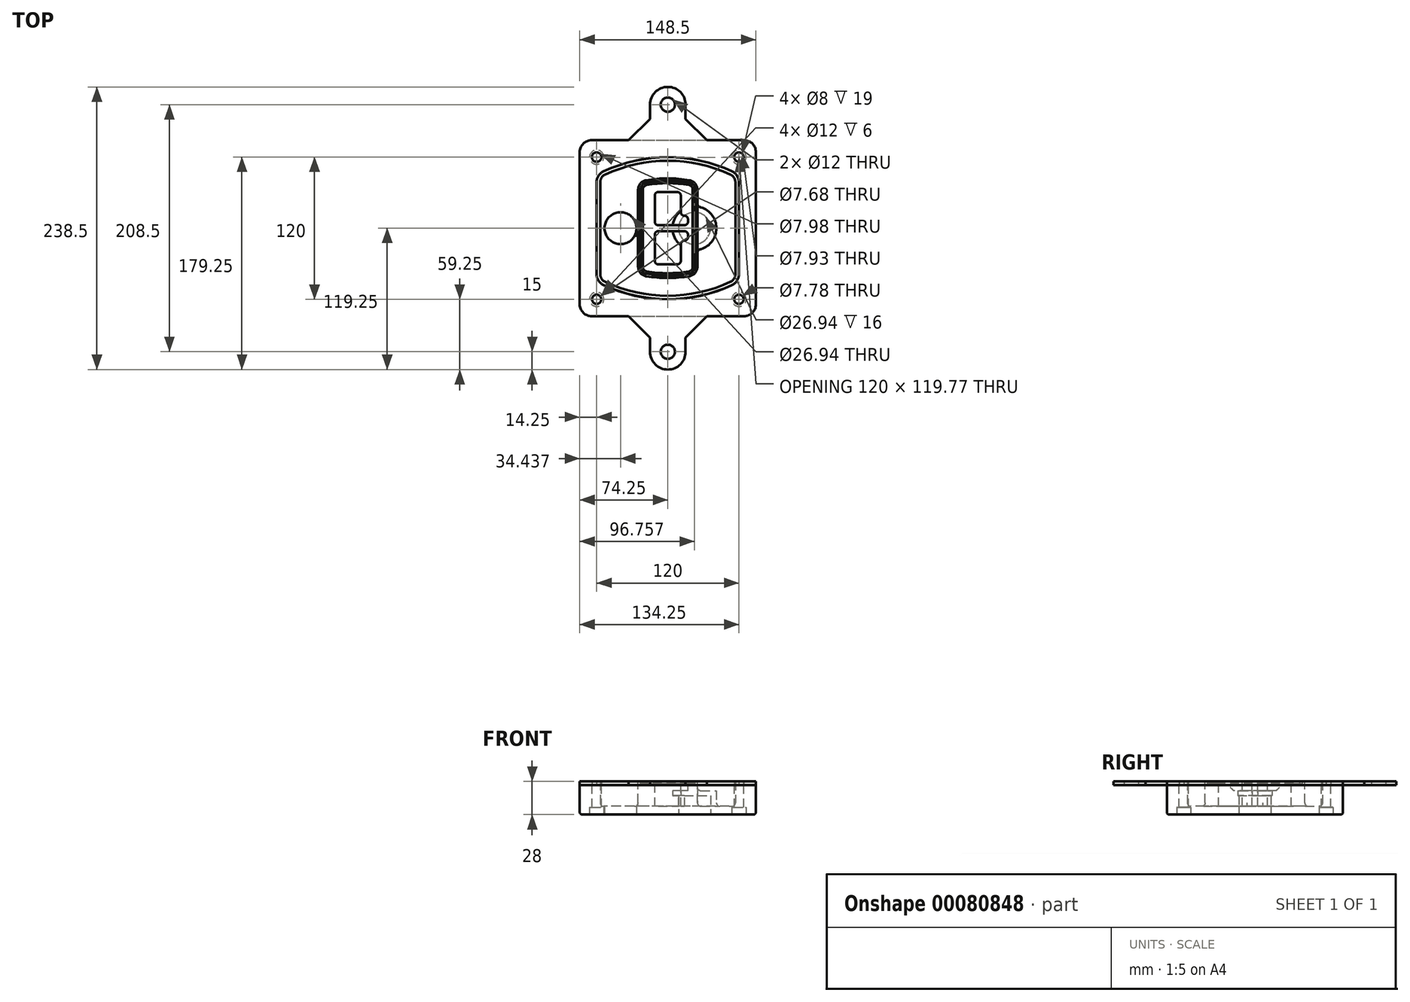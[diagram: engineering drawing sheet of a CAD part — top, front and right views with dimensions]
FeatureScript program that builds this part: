
annotation { "Feature Type Name" : "Feature", "Feature Type Description" : "" }
export const myFeature = defineFeature(function(context is Context, id is Id, definition is map)
    precondition{}
    {
        {
            var Q0;
            Q0=qCreatedBy(makeId("Top.planeOp"),FACE);
            var sketch = newSketch(context, id + "F0", { "sketchPlane" : qUnion([Q0])});
            skPoint(sketch, "E0.rect.middle", {"position": v(0, 0) * mm});
            skLineSegment(sketch, "E1.bottom", {"start": v(-64.25, -74.25) * mm, "end": v(64.25, -74.25) * mm});
            skLineSegment(sketch, "E1.top", {"start": v(-64.25, 74.25) * mm, "end": v(64.25, 74.25) * mm});
            skLineSegment(sketch, "E1.left", {"start": v(-74.25, -64.25) * mm, "end": v(-74.25, 64.25) * mm});
            skLineSegment(sketch, "E1.right", {"start": v(74.25, -64.25) * mm, "end": v(74.25, 64.25) * mm});
            skLineSegment(sketch, "E2", {"start": v(-74.25, 74.25) * mm, "end": v(74.25, -74.25) * mm, "construction": true});
            skLineSegment(sketch, "E3", {"start": v(74.25, 74.25) * mm, "end": v(-74.25, -74.25) * mm, "construction": true});
            skCircle(sketch, "E4", {"center": v(-60, 60) * mm, "radius": 4 * mm});
            skCircle(sketch, "E5", {"center": v(60, 60) * mm, "radius": 4 * mm});
            skCircle(sketch, "E6", {"center": v(60, -60) * mm, "radius": 4 * mm});
            skCircle(sketch, "E7", {"center": v(-60, -60) * mm, "radius": 4 * mm});
            skLineSegment(sketch, "E8", {"start": v(-60, 60) * mm, "end": v(60, 60) * mm, "construction": true});
            skLineSegment(sketch, "E9", {"start": v(60, 60) * mm, "end": v(60, -60) * mm, "construction": true});
            skLineSegment(sketch, "E10", {"start": v(60, -60) * mm, "end": v(-60, -60) * mm, "construction": true});
            skLineSegment(sketch, "E11", {"start": v(-60, -60) * mm, "end": v(-60, 60) * mm, "construction": true});
            skLineSegment(sketch, "E12", {"start": v(-60, 38.83) * mm, "end": v(-60, -38.83) * mm});
            skLineSegment(sketch, "E13", {"start": v(60, 38.83) * mm, "end": v(60, -38.83) * mm});
            skArc(sketch, "E14", {"start": v(54.26, 47.88) * mm, "mid": v(0, 60) * mm, "end": v(-54.26, 47.88) * mm});
            skArc(sketch, "E15", {"start": v(-54.26, -47.88) * mm, "mid": v(0, -60) * mm, "end": v(54.26, -47.88) * mm});
            skLineSegment(sketch, "E16", {"start": v(-60, 0) * mm, "end": v(60, 0) * mm, "construction": true});
            skPoint(sketch, "E17.visualSharp", {"position": v(-60, -45) * mm});
            skArc(sketch, "E17.filletArc", {"start": v(-60, -38.83) * mm, "mid": v(-58.44, -44.2) * mm, "end": v(-54.26, -47.88) * mm});
            skPoint(sketch, "E18.visualSharp", {"position": v(-60, 45) * mm});
            skArc(sketch, "E18.filletArc", {"start": v(-54.26, 47.88) * mm, "mid": v(-58.44, 44.2) * mm, "end": v(-60, 38.83) * mm});
            skPoint(sketch, "E19.visualSharp", {"position": v(60, 45) * mm});
            skArc(sketch, "E19.filletArc", {"start": v(60, 38.83) * mm, "mid": v(58.44, 44.2) * mm, "end": v(54.26, 47.88) * mm});
            skPoint(sketch, "E20.visualSharp", {"position": v(60, -45) * mm});
            skArc(sketch, "E20.filletArc", {"start": v(54.26, -47.88) * mm, "mid": v(58.44, -44.2) * mm, "end": v(60, -38.83) * mm});
            skPoint(sketch, "E21.visualSharp", {"position": v(-74.25, 74.25) * mm});
            skArc(sketch, "E21.filletArc", {"start": v(-64.25, 74.25) * mm, "mid": v(-71.32, 71.32) * mm, "end": v(-74.25, 64.25) * mm});
            skPoint(sketch, "E22.visualSharp", {"position": v(74.25, 74.25) * mm});
            skArc(sketch, "E22.filletArc", {"start": v(74.25, 64.25) * mm, "mid": v(71.32, 71.32) * mm, "end": v(64.25, 74.25) * mm});
            skPoint(sketch, "E23.visualSharp", {"position": v(74.25, -74.25) * mm});
            skArc(sketch, "E23.filletArc", {"start": v(64.25, -74.25) * mm, "mid": v(71.32, -71.32) * mm, "end": v(74.25, -64.25) * mm});
            skPoint(sketch, "E24.visualSharp", {"position": v(-74.25, -74.25) * mm});
            skArc(sketch, "E24.filletArc", {"start": v(-74.25, -64.25) * mm, "mid": v(-71.32, -71.32) * mm, "end": v(-64.25, -74.25) * mm});
            skArc(sketch, "E25.0", {"start": v(57, 38.83) * mm, "mid": v(55.9, 42.58) * mm, "end": v(52.98, 45.17) * mm});
            skLineSegment(sketch, "E25.1", {"start": v(57, 38.83) * mm, "end": v(57, -38.83) * mm});
            skArc(sketch, "E25.2", {"start": v(52.98, -45.17) * mm, "mid": v(55.9, -42.58) * mm, "end": v(57, -38.83) * mm});
            skArc(sketch, "E25.3", {"start": v(-52.98, -45.17) * mm, "mid": v(0, -57) * mm, "end": v(52.98, -45.17) * mm});
            skArc(sketch, "E25.4", {"start": v(-57, -38.83) * mm, "mid": v(-55.9, -42.58) * mm, "end": v(-52.98, -45.17) * mm});
            skArc(sketch, "E25.5", {"start": v(52.98, 45.17) * mm, "mid": v(0, 57) * mm, "end": v(-52.98, 45.17) * mm});
            skLineSegment(sketch, "E25.6", {"start": v(-57, 38.83) * mm, "end": v(-57, -38.83) * mm});
            skArc(sketch, "E25.7", {"start": v(-52.98, 45.17) * mm, "mid": v(-55.9, 42.58) * mm, "end": v(-57, 38.83) * mm});
            skArc(sketch, "E26.0", {"start": v(-55.96, 51.5) * mm, "mid": v(-61.82, 46.33) * mm, "end": v(-64, 38.83) * mm});
            skArc(sketch, "E26.1", {"start": v(55.96, 51.5) * mm, "mid": v(0, 64) * mm, "end": v(-55.96, 51.5) * mm});
            skArc(sketch, "E26.2", {"start": v(64, 38.83) * mm, "mid": v(61.82, 46.33) * mm, "end": v(55.96, 51.5) * mm});
            skLineSegment(sketch, "E26.3", {"start": v(64, 38.83) * mm, "end": v(64, -38.83) * mm});
            skArc(sketch, "E26.4", {"start": v(55.96, -51.5) * mm, "mid": v(61.82, -46.33) * mm, "end": v(64, -38.83) * mm});
            skLineSegment(sketch, "E26.5", {"start": v(-64, 38.83) * mm, "end": v(-64, -38.83) * mm});
            skArc(sketch, "E26.6", {"start": v(-55.96, -51.5) * mm, "mid": v(0, -64) * mm, "end": v(55.96, -51.5) * mm});
            skArc(sketch, "E26.7", {"start": v(-64, -38.83) * mm, "mid": v(-61.82, -46.33) * mm, "end": v(-55.96, -51.5) * mm});
            skSolve(sketch);
        }
        {
            var Q0;
            Q0=makeQuery(id+"F0.imprint","IMPRINT",FACE,{"disambiguationData":[TD([[makeQuery(id+"F0.imprint","IMPRINT",EDGE,{"derivedFrom":sQuery(id+"F0.wireOp",EDGE,"E1.bottom")}),1.0]])]});
            var Q1;
            Q1=makeQuery(id+"F0.imprint","IMPRINT",FACE,{"disambiguationData":[TD([[makeQuery(id+"F0.imprint","IMPRINT",EDGE,{"derivedFrom":sQuery(id+"F0.wireOp",EDGE,"E12")}),1.0]])]});
            var Q2;
            Q2=makeQuery(id+"F0.imprint","IMPRINT",FACE,{"disambiguationData":[TD([[makeQuery(id+"F0.imprint","IMPRINT",EDGE,{"derivedFrom":sQuery(id+"F0.wireOp",EDGE,"E25.0")}),1.0]])]});
            var Q3;
            Q3=makeQuery(id+"F0.imprint","IMPRINT",FACE,{"disambiguationData":[TD([[makeQuery(id+"F0.imprint","IMPRINT",EDGE,{"derivedFrom":sQuery(id+"F0.wireOp",EDGE,"E12")}),-1.0]])]});
            extrude(context, id + "F1", {"entities" : qUnion([Q0, Q1, Q2, Q3]), "oppositeDirection" : true, "depth" : 25 * mm});
        }
        {
            var Q0;
            Q0=makeQuery(id+"F0.imprint","IMPRINT",FACE,{"disambiguationData":[TD([[makeQuery(id+"F0.imprint","IMPRINT",EDGE,{"derivedFrom":sQuery(id+"F0.wireOp",EDGE,"E12")}),1.0]])]});
            extrude(context, id + "F2", {"entities" : qUnion([Q0]), "operationType" : NewBodyOperationType.ADD, "depth" : 3 * mm});
        }
        {
            var Q0;
            Q0=makeQuery(id+"F0.imprint","IMPRINT",FACE,{"disambiguationData":[TD([[makeQuery(id+"F0.imprint","IMPRINT",EDGE,{"derivedFrom":sQuery(id+"F0.wireOp",EDGE,"E25.0")}),1.0]])]});
            extrude(context, id + "F3", {"entities" : qUnion([Q0]), "operationType" : NewBodyOperationType.REMOVE, "oppositeDirection" : true, "depth" : 18 * mm});
        }
        {
            var Q0;
            Q0=makeQuery(id+"F2.opExtrude","CAP_FACE",FACE,{"disambiguationData":[OSD([sQuery(id+"F0.wireOp",EDGE,"E12"),sQuery(id+"F0.wireOp",EDGE,"E13"),sQuery(id+"F0.wireOp",EDGE,"E14"),sQuery(id+"F0.wireOp",EDGE,"E15"),sQuery(id+"F0.wireOp",EDGE,"E17.filletArc"),sQuery(id+"F0.wireOp",EDGE,"E18.filletArc"),sQuery(id+"F0.wireOp",EDGE,"E19.filletArc"),sQuery(id+"F0.wireOp",EDGE,"E20.filletArc"),sQuery(id+"F0.wireOp",EDGE,"E25.0"),sQuery(id+"F0.wireOp",EDGE,"E25.1"),sQuery(id+"F0.wireOp",EDGE,"E25.2"),sQuery(id+"F0.wireOp",EDGE,"E25.3"),sQuery(id+"F0.wireOp",EDGE,"E25.4"),sQuery(id+"F0.wireOp",EDGE,"E25.5"),sQuery(id+"F0.wireOp",EDGE,"E25.6"),sQuery(id+"F0.wireOp",EDGE,"E25.7")])],"isStart":false});
            var sketch = newSketch(context, id + "F4", { "sketchPlane" : qUnion([Q0])});
            skArc(sketch, "E27.0", {"start": v(-18.34, -40.45) * mm, "mid": v(0, -42) * mm, "end": v(18.34, -40.45) * mm});
            skArc(sketch, "E28.0", {"start": v(18.34, 40.45) * mm, "mid": v(0, 42) * mm, "end": v(-18.34, 40.45) * mm});
            skLineSegment(sketch, "E29", {"start": v(-25, 32.57) * mm, "end": v(-25, -32.57) * mm});
            skLineSegment(sketch, "E30", {"start": v(25, 32.57) * mm, "end": v(25, -32.57) * mm});
            skLineSegment(sketch, "E31", {"start": v(-25, 39.1) * mm, "end": v(25, 39.1) * mm, "construction": true});
            skLineSegment(sketch, "E32", {"start": v(-25, -39.1) * mm, "end": v(25, -39.1) * mm, "construction": true});
            skPoint(sketch, "E33.visualSharp", {"position": v(-25, 39.1) * mm});
            skArc(sketch, "E33.filletArc", {"start": v(-18.34, 40.45) * mm, "mid": v(-23.11, 37.73) * mm, "end": v(-25, 32.57) * mm});
            skPoint(sketch, "E34.visualSharp", {"position": v(25, 39.1) * mm});
            skArc(sketch, "E34.filletArc", {"start": v(25, 32.57) * mm, "mid": v(23.11, 37.73) * mm, "end": v(18.34, 40.45) * mm});
            skPoint(sketch, "E35.visualSharp", {"position": v(25, -39.1) * mm});
            skArc(sketch, "E35.filletArc", {"start": v(18.34, -40.45) * mm, "mid": v(23.11, -37.73) * mm, "end": v(25, -32.57) * mm});
            skPoint(sketch, "E36.visualSharp", {"position": v(-25, -39.1) * mm});
            skArc(sketch, "E36.filletArc", {"start": v(-25, -32.57) * mm, "mid": v(-23.11, -37.73) * mm, "end": v(-18.34, -40.45) * mm});
            skArc(sketch, "E37.0", {"start": v(52.98, 45.17) * mm, "mid": v(0, 57) * mm, "end": v(-52.98, 45.17) * mm});
            skArc(sketch, "E37.1", {"start": v(-52.98, 45.17) * mm, "mid": v(-55.9, 42.58) * mm, "end": v(-57, 38.83) * mm});
            skLineSegment(sketch, "E37.2", {"start": v(-57, 38.83) * mm, "end": v(-57, -38.83) * mm});
            skArc(sketch, "E37.3", {"start": v(-57, -38.83) * mm, "mid": v(-55.9, -42.58) * mm, "end": v(-52.98, -45.17) * mm});
            skArc(sketch, "E37.4", {"start": v(-52.98, -45.17) * mm, "mid": v(0, -57) * mm, "end": v(52.98, -45.17) * mm});
            skArc(sketch, "E37.5", {"start": v(52.98, -45.17) * mm, "mid": v(55.9, -42.58) * mm, "end": v(57, -38.83) * mm});
            skLineSegment(sketch, "E37.6", {"start": v(57, 38.83) * mm, "end": v(57, -38.83) * mm});
            skArc(sketch, "E37.7", {"start": v(57, 38.83) * mm, "mid": v(55.9, 42.58) * mm, "end": v(52.98, 45.17) * mm});
            skLineSegment(sketch, "E38.0", {"start": v(23, 32.57) * mm, "end": v(23, -32.57) * mm});
            skArc(sketch, "E38.1", {"start": v(18, -38.48) * mm, "mid": v(21.58, -36.44) * mm, "end": v(23, -32.57) * mm});
            skArc(sketch, "E38.2", {"start": v(-18, -38.48) * mm, "mid": v(0, -40) * mm, "end": v(18, -38.48) * mm});
            skArc(sketch, "E38.3", {"start": v(-23, -32.57) * mm, "mid": v(-21.58, -36.44) * mm, "end": v(-18, -38.48) * mm});
            skLineSegment(sketch, "E38.4", {"start": v(-23, 32.57) * mm, "end": v(-23, -32.57) * mm});
            skArc(sketch, "E38.5", {"start": v(23, 32.57) * mm, "mid": v(21.58, 36.44) * mm, "end": v(18, 38.48) * mm});
            skArc(sketch, "E38.6", {"start": v(-18, 38.48) * mm, "mid": v(-21.58, 36.44) * mm, "end": v(-23, 32.57) * mm});
            skArc(sketch, "E38.7", {"start": v(18, 38.48) * mm, "mid": v(0, 40) * mm, "end": v(-18, 38.48) * mm});
            skArc(sketch, "E39.0", {"start": v(21, 32.57) * mm, "mid": v(20.06, 35.15) * mm, "end": v(17.67, 36.5) * mm});
            skLineSegment(sketch, "E39.1", {"start": v(21, 32.57) * mm, "end": v(21, -32.57) * mm});
            skArc(sketch, "E39.2", {"start": v(17.67, -36.5) * mm, "mid": v(20.06, -35.15) * mm, "end": v(21, -32.57) * mm});
            skArc(sketch, "E39.3", {"start": v(-17.67, -36.5) * mm, "mid": v(0, -38) * mm, "end": v(17.67, -36.5) * mm});
            skArc(sketch, "E39.4", {"start": v(-21, -32.57) * mm, "mid": v(-20.06, -35.15) * mm, "end": v(-17.67, -36.5) * mm});
            skArc(sketch, "E39.5", {"start": v(17.67, 36.5) * mm, "mid": v(0, 38) * mm, "end": v(-17.67, 36.5) * mm});
            skLineSegment(sketch, "E39.6", {"start": v(-21, 32.57) * mm, "end": v(-21, -32.57) * mm});
            skArc(sketch, "E39.7", {"start": v(-17.67, 36.5) * mm, "mid": v(-20.06, 35.15) * mm, "end": v(-21, 32.57) * mm});
            skLineSegment(sketch, "E40", {"start": v(-25, 0) * mm, "end": v(25, 0) * mm, "construction": true});
            skLineSegment(sketch, "E41", {"start": v(-11, 5.5) * mm, "end": v(-11, 27.5) * mm});
            skLineSegment(sketch, "E42", {"start": v(-8, 30.5) * mm, "end": v(8, 30.5) * mm});
            skLineSegment(sketch, "E43", {"start": v(11, 27.5) * mm, "end": v(11, 13.5) * mm});
            skLineSegment(sketch, "E44", {"start": v(14, 10.5) * mm, "end": v(14, 10.5) * mm});
            skLineSegment(sketch, "E45", {"start": v(17, 7.5) * mm, "end": v(17, 5.5) * mm});
            skLineSegment(sketch, "E46", {"start": v(14, 2.5) * mm, "end": v(-8, 2.5) * mm});
            skPoint(sketch, "E47.visualSharp", {"position": v(-11, 30.5) * mm});
            skArc(sketch, "E47.filletArc", {"start": v(-8, 30.5) * mm, "mid": v(-10.12, 29.62) * mm, "end": v(-11, 27.5) * mm});
            skPoint(sketch, "E48.visualSharp", {"position": v(11, 30.5) * mm});
            skArc(sketch, "E48.filletArc", {"start": v(11, 27.5) * mm, "mid": v(10.12, 29.62) * mm, "end": v(8, 30.5) * mm});
            skPoint(sketch, "E49.visualSharp", {"position": v(11, 10.5) * mm});
            skArc(sketch, "E49.filletArc", {"start": v(11, 13.5) * mm, "mid": v(11.88, 11.38) * mm, "end": v(14, 10.5) * mm});
            skPoint(sketch, "E50.visualSharp", {"position": v(17, 10.5) * mm});
            skArc(sketch, "E50.filletArc", {"start": v(17, 7.5) * mm, "mid": v(16.12, 9.62) * mm, "end": v(14, 10.5) * mm});
            skPoint(sketch, "E51.visualSharp", {"position": v(17, 2.5) * mm});
            skArc(sketch, "E51.filletArc", {"start": v(14, 2.5) * mm, "mid": v(16.12, 3.38) * mm, "end": v(17, 5.5) * mm});
            skPoint(sketch, "E52.visualSharp", {"position": v(-11, 2.5) * mm});
            skArc(sketch, "E52.filletArc", {"start": v(-11, 5.5) * mm, "mid": v(-10.12, 3.38) * mm, "end": v(-8, 2.5) * mm});
            skLineSegment(sketch, "E53.0.MirrorCS", {"start": v(14, -2.5) * mm, "end": v(-8, -2.5) * mm});
            skArc(sketch, "E54.0.MirrorCS", {"start": v(-11, -5.5) * mm, "mid": v(-10.12, -3.38) * mm, "end": v(-8, -2.5) * mm});
            skLineSegment(sketch, "E55.0.MirrorCS", {"start": v(-11, -5.5) * mm, "end": v(-11, -27.5) * mm});
            skArc(sketch, "E56.0.MirrorCS", {"start": v(-8, -30.5) * mm, "mid": v(-10.12, -29.62) * mm, "end": v(-11, -27.5) * mm});
            skLineSegment(sketch, "E57.0.MirrorCS", {"start": v(-8, -30.5) * mm, "end": v(8, -30.5) * mm});
            skArc(sketch, "E58.0.MirrorCS", {"start": v(11, -27.5) * mm, "mid": v(10.12, -29.62) * mm, "end": v(8, -30.5) * mm});
            skLineSegment(sketch, "E59.0.MirrorCS", {"start": v(11, -27.5) * mm, "end": v(11, -13.5) * mm});
            skArc(sketch, "E60.0.MirrorCS", {"start": v(11, -13.5) * mm, "mid": v(11.88, -11.38) * mm, "end": v(14, -10.5) * mm});
            skArc(sketch, "E61.0.MirrorCS", {"start": v(17, -7.5) * mm, "mid": v(16.12, -9.62) * mm, "end": v(14, -10.5) * mm});
            skLineSegment(sketch, "E62.0.MirrorCS", {"start": v(17, -7.5) * mm, "end": v(17, -5.5) * mm});
            skArc(sketch, "E63.0.MirrorCS", {"start": v(14, -2.5) * mm, "mid": v(16.12, -3.38) * mm, "end": v(17, -5.5) * mm});
            skSolve(sketch);
        }
        {
            var Q0;
            Q0=makeQuery(id+"F4.imprint","IMPRINT",FACE,{"disambiguationData":[TD([[makeQuery(id+"F4.imprint","IMPRINT",EDGE,{"derivedFrom":sQuery(id+"F4.wireOp",EDGE,"E27.0")}),1.0]])]});
            var Q1;
            Q1=makeQuery(id+"F4.imprint","IMPRINT",FACE,{"disambiguationData":[TD([[makeQuery(id+"F4.imprint","IMPRINT",EDGE,{"derivedFrom":sQuery(id+"F4.wireOp",EDGE,"E38.0")}),-1.0]])]});
            var Q2;
            Q2=makeQuery(id+"F4.imprint","IMPRINT",FACE,{"disambiguationData":[TD([[makeQuery(id+"F4.imprint","IMPRINT",EDGE,{"derivedFrom":sQuery(id+"F4.wireOp",EDGE,"E39.0")}),1.0]])]});
            extrude(context, id + "F5", {"entities" : qUnion([Q0, Q1, Q2]), "operationType" : NewBodyOperationType.ADD, "endBound" : BoundingType.UP_TO_NEXT, "oppositeDirection" : true, "depth" : 25 * mm});
        }
        {
            var Q0;
            Q0=makeQuery(id+"F4.imprint","IMPRINT",FACE,{"disambiguationData":[TD([[makeQuery(id+"F4.imprint","IMPRINT",EDGE,{"derivedFrom":sQuery(id+"F4.wireOp",EDGE,"E38.0")}),-1.0]])]});
            extrude(context, id + "F6", {"entities" : qUnion([Q0]), "operationType" : NewBodyOperationType.REMOVE, "oppositeDirection" : true, "depth" : 2 * mm});
        }
        {
            var Q0;
            Q0=makeQuery(id+"F1.opExtrude","CAP_FACE",FACE,{"disambiguationData":[OSD([sQuery(id+"F0.wireOp",EDGE,"E1.bottom"),sQuery(id+"F0.wireOp",EDGE,"E1.top"),sQuery(id+"F0.wireOp",EDGE,"E1.left"),sQuery(id+"F0.wireOp",EDGE,"E1.right"),sQuery(id+"F0.wireOp",EDGE,"E4"),sQuery(id+"F0.wireOp",EDGE,"E5"),sQuery(id+"F0.wireOp",EDGE,"E6"),sQuery(id+"F0.wireOp",EDGE,"E7"),sQuery(id+"F0.wireOp",EDGE,"E21.filletArc"),sQuery(id+"F0.wireOp",EDGE,"E22.filletArc"),sQuery(id+"F0.wireOp",EDGE,"E23.filletArc"),sQuery(id+"F0.wireOp",EDGE,"E24.filletArc")])],"isStart":false});
            var sketch = newSketch(context, id + "F7", { "sketchPlane" : qUnion([Q0])});
            skCircle(sketch, "E64", {"center": v(22.5, 0) * mm, "radius": 13.47 * mm});
            skCircle(sketch, "E65", {"center": v(-39.81, 0) * mm, "radius": 13.47 * mm});
            skLineSegment(sketch, "E66", {"start": v(74.25, 0) * mm, "end": v(-74.25, 0) * mm});
            skCircle(sketch, "E67", {"center": v(22.5, 0) * mm, "radius": 18.47 * mm});
            skCircle(sketch, "E68", {"center": v(60, -60) * mm, "radius": 6 * mm});
            skCircle(sketch, "E69", {"center": v(-60, -60) * mm, "radius": 6 * mm});
            skCircle(sketch, "E70", {"center": v(-60, 60) * mm, "radius": 6 * mm});
            skCircle(sketch, "E71", {"center": v(60, 60) * mm, "radius": 6 * mm});
            skSolve(sketch);
        }
        {
            var Q0;
            {var subQ1=sQuery(id+"F7.wireOp",EDGE,"E66");var subQ4=sQuery(id+"F7.wireOp",EDGE,"E64");var subQ6=makeQuery(id+"F7.imprint","INTERSECT",VERTEX,{"disambiguationData":[OD(0.0)],"derivedFrom":[subQ4,subQ1]});Q0=makeQuery(id+"F7.imprint","IMPRINT",FACE,{"disambiguationData":[TD([[makeQuery(id+"F7.imprint","IMPRINT",EDGE,{"disambiguationData":[TD([[subQ6,-1.0]])],"derivedFrom":subQ4}),-1.0]])]});}
            var Q1;
            {var subQ0=sQuery(id+"F7.wireOp",EDGE,"E66");var subQ1=sQuery(id+"F7.wireOp",EDGE,"E64");var subQ3=makeQuery(id+"F7.imprint","INTERSECT",VERTEX,{"disambiguationData":[OD(0.0)],"derivedFrom":[subQ1,subQ0]});Q1=makeQuery(id+"F7.imprint","IMPRINT",FACE,{"disambiguationData":[TD([[makeQuery(id+"F7.imprint","IMPRINT",EDGE,{"disambiguationData":[TD([[subQ3,-1.0]])],"derivedFrom":subQ1}),1.0]])]});}
            var Q2;
            {var subQ0=sQuery(id+"F7.wireOp",EDGE,"E66");var subQ1=sQuery(id+"F7.wireOp",EDGE,"E64");var subQ3=makeQuery(id+"F7.imprint","INTERSECT",VERTEX,{"disambiguationData":[OD(0.0)],"derivedFrom":[subQ1,subQ0]});Q2=makeQuery(id+"F7.imprint","IMPRINT",FACE,{"disambiguationData":[TD([[makeQuery(id+"F7.imprint","IMPRINT",EDGE,{"disambiguationData":[TD([[subQ3,1.0]])],"derivedFrom":subQ1}),1.0]])]});}
            var Q3;
            {var subQ1=sQuery(id+"F7.wireOp",EDGE,"E66");var subQ4=sQuery(id+"F7.wireOp",EDGE,"E64");var subQ6=makeQuery(id+"F7.imprint","INTERSECT",VERTEX,{"disambiguationData":[OD(0.0)],"derivedFrom":[subQ4,subQ1]});Q3=makeQuery(id+"F7.imprint","IMPRINT",FACE,{"disambiguationData":[TD([[makeQuery(id+"F7.imprint","IMPRINT",EDGE,{"disambiguationData":[TD([[subQ6,1.0]])],"derivedFrom":subQ4}),-1.0]])]});}
            extrude(context, id + "F8", {"entities" : qUnion([Q0, Q1, Q2, Q3]), "operationType" : NewBodyOperationType.ADD, "oppositeDirection" : true, "depth" : 20 * mm});
        }
        {
            var Q0;
            {var subQ0=sQuery(id+"F7.wireOp",EDGE,"E66");var subQ1=sQuery(id+"F7.wireOp",EDGE,"E64");var subQ3=makeQuery(id+"F7.imprint","INTERSECT",VERTEX,{"disambiguationData":[OD(0.0)],"derivedFrom":[subQ1,subQ0]});Q0=makeQuery(id+"F7.imprint","IMPRINT",FACE,{"disambiguationData":[TD([[makeQuery(id+"F7.imprint","IMPRINT",EDGE,{"disambiguationData":[TD([[subQ3,-1.0]])],"derivedFrom":subQ1}),1.0]])]});}
            var Q1;
            {var subQ0=sQuery(id+"F7.wireOp",EDGE,"E66");var subQ1=sQuery(id+"F7.wireOp",EDGE,"E64");var subQ3=makeQuery(id+"F7.imprint","INTERSECT",VERTEX,{"disambiguationData":[OD(0.0)],"derivedFrom":[subQ1,subQ0]});Q1=makeQuery(id+"F7.imprint","IMPRINT",FACE,{"disambiguationData":[TD([[makeQuery(id+"F7.imprint","IMPRINT",EDGE,{"disambiguationData":[TD([[subQ3,1.0]])],"derivedFrom":subQ1}),1.0]])]});}
            extrude(context, id + "F9", {"entities" : qUnion([Q0, Q1]), "operationType" : NewBodyOperationType.REMOVE, "oppositeDirection" : true, "depth" : 16 * mm});
        }
        {
            var Q0;
            {var subQ0=sQuery(id+"F7.wireOp",EDGE,"E66");var subQ1=sQuery(id+"F7.wireOp",EDGE,"E65");var subQ3=makeQuery(id+"F7.imprint","INTERSECT",VERTEX,{"disambiguationData":[OD(0.0)],"derivedFrom":[subQ1,subQ0]});Q0=makeQuery(id+"F7.imprint","IMPRINT",FACE,{"disambiguationData":[TD([[makeQuery(id+"F7.imprint","IMPRINT",EDGE,{"disambiguationData":[TD([[subQ3,-1.0]])],"derivedFrom":subQ1}),1.0]])]});}
            var Q1;
            {var subQ0=sQuery(id+"F7.wireOp",EDGE,"E66");var subQ1=sQuery(id+"F7.wireOp",EDGE,"E65");var subQ3=makeQuery(id+"F7.imprint","INTERSECT",VERTEX,{"disambiguationData":[OD(0.0)],"derivedFrom":[subQ1,subQ0]});Q1=makeQuery(id+"F7.imprint","IMPRINT",FACE,{"disambiguationData":[TD([[makeQuery(id+"F7.imprint","IMPRINT",EDGE,{"disambiguationData":[TD([[subQ3,1.0]])],"derivedFrom":subQ1}),1.0]])]});}
            extrude(context, id + "F10", {"entities" : qUnion([Q0, Q1]), "operationType" : NewBodyOperationType.REMOVE, "oppositeDirection" : true, "depth" : 25 * mm});
        }
        {
            var Q0;
            Q0=makeQuery(id+"F7.imprint","IMPRINT",FACE,{"disambiguationData":[TD([[makeQuery(id+"F7.imprint","IMPRINT",EDGE,{"derivedFrom":sQuery(id+"F7.wireOp",EDGE,"E68")}),1.0]])]});
            var Q1;
            Q1=makeQuery(id+"F7.imprint","IMPRINT",FACE,{"disambiguationData":[TD([[makeQuery(id+"F7.imprint","IMPRINT",EDGE,{"derivedFrom":makeQuery(id+"F1.opExtrude","CAP_EDGE",EDGE,{"disambiguationData":[OSD([sQuery(id+"F0.wireOp",EDGE,"E5")])],"isStart":false})}),-1.0]])]});
            var Q2;
            Q2=makeQuery(id+"F7.imprint","IMPRINT",FACE,{"disambiguationData":[TD([[makeQuery(id+"F7.imprint","IMPRINT",EDGE,{"derivedFrom":sQuery(id+"F7.wireOp",EDGE,"E69")}),1.0]])]});
            var Q3;
            Q3=makeQuery(id+"F7.imprint","IMPRINT",FACE,{"disambiguationData":[TD([[makeQuery(id+"F7.imprint","IMPRINT",EDGE,{"derivedFrom":makeQuery(id+"F1.opExtrude","CAP_EDGE",EDGE,{"disambiguationData":[OSD([sQuery(id+"F0.wireOp",EDGE,"E4")])],"isStart":false})}),-1.0]])]});
            var Q4;
            Q4=makeQuery(id+"F7.imprint","IMPRINT",FACE,{"disambiguationData":[TD([[makeQuery(id+"F7.imprint","IMPRINT",EDGE,{"derivedFrom":sQuery(id+"F7.wireOp",EDGE,"E70")}),1.0]])]});
            var Q5;
            Q5=makeQuery(id+"F7.imprint","IMPRINT",FACE,{"disambiguationData":[TD([[makeQuery(id+"F7.imprint","IMPRINT",EDGE,{"derivedFrom":makeQuery(id+"F1.opExtrude","CAP_EDGE",EDGE,{"disambiguationData":[OSD([sQuery(id+"F0.wireOp",EDGE,"E7")])],"isStart":false})}),-1.0]])]});
            var Q6;
            Q6=makeQuery(id+"F7.imprint","IMPRINT",FACE,{"disambiguationData":[TD([[makeQuery(id+"F7.imprint","IMPRINT",EDGE,{"derivedFrom":sQuery(id+"F7.wireOp",EDGE,"E71")}),1.0]])]});
            var Q7;
            Q7=makeQuery(id+"F7.imprint","IMPRINT",FACE,{"disambiguationData":[TD([[makeQuery(id+"F7.imprint","IMPRINT",EDGE,{"derivedFrom":makeQuery(id+"F1.opExtrude","CAP_EDGE",EDGE,{"disambiguationData":[OSD([sQuery(id+"F0.wireOp",EDGE,"E6")])],"isStart":false})}),-1.0]])]});
            extrude(context, id + "F11", {"entities" : qUnion([Q0, Q1, Q2, Q3, Q4, Q5, Q6, Q7]), "operationType" : NewBodyOperationType.REMOVE, "oppositeDirection" : true, "depth" : 6 * mm});
        }
        {
            var Q0;
            Q0=makeQuery(id+"F9.boolean.opBoolean","COPY",FACE,{"derivedFrom":makeQuery(id+"F9.opExtrude","CAP_FACE",FACE,{"disambiguationData":[OSD([sQuery(id+"F7.wireOp",EDGE,"E64")])],"isStart":false})});
            var sketch = newSketch(context, id + "F12", { "sketchPlane" : qUnion([Q0])});
            skArc(sketch, "E72.0", {"start": v(11, 14.45) * mm, "mid": v(6.45, 9.13) * mm, "end": v(4.2, 2.5) * mm});
            skArc(sketch, "E72.1", {"start": v(4.2, -2.5) * mm, "mid": v(6.45, -9.13) * mm, "end": v(11, -14.45) * mm});
            skLineSegment(sketch, "E73", {"start": v(4.2, -2.5) * mm, "end": v(14, -2.5) * mm});
            skLineSegment(sketch, "E74.0", {"start": v(14, 2.5) * mm, "end": v(4.2, 2.5) * mm});
            skArc(sketch, "E74.1", {"start": v(14, 2.5) * mm, "mid": v(16.12, 3.38) * mm, "end": v(17, 5.5) * mm});
            skLineSegment(sketch, "E74.2", {"start": v(17, 7.5) * mm, "end": v(17, 5.5) * mm});
            skArc(sketch, "E74.3", {"start": v(17, 7.5) * mm, "mid": v(16.12, 9.62) * mm, "end": v(14, 10.5) * mm});
            skArc(sketch, "E74.4", {"start": v(11, 13.5) * mm, "mid": v(11.88, 11.38) * mm, "end": v(14, 10.5) * mm});
            skLineSegment(sketch, "E74.5", {"start": v(11, 14.45) * mm, "end": v(11, 13.5) * mm});
            skLineSegment(sketch, "E74.7", {"start": v(14, -2.5) * mm, "end": v(4.2, -2.5) * mm});
            skArc(sketch, "E74.8", {"start": v(14, -2.5) * mm, "mid": v(16.12, -3.38) * mm, "end": v(17, -5.5) * mm});
            skLineSegment(sketch, "E74.9", {"start": v(17, -7.5) * mm, "end": v(17, -5.5) * mm});
            skArc(sketch, "E74.10", {"start": v(17, -7.5) * mm, "mid": v(16.12, -9.62) * mm, "end": v(14, -10.5) * mm});
            skArc(sketch, "E74.11", {"start": v(11, -13.5) * mm, "mid": v(11.88, -11.38) * mm, "end": v(14, -10.5) * mm});
            skLineSegment(sketch, "E74.12", {"start": v(11, -14.45) * mm, "end": v(11, -13.5) * mm});
            skPoint(sketch, "E75.orphan", {"position": v(11, -27.5) * mm});
            skPoint(sketch, "E76.orphan", {"position": v(-8, -2.5) * mm});
            skPoint(sketch, "E77.orphan", {"position": v(-8, 2.5) * mm});
            skPoint(sketch, "E78.orphan", {"position": v(11, 27.5) * mm});
            skSolve(sketch);
        }
        {
            var Q0;
            {var subQ7=sQuery(id+"F12.wireOp",EDGE,"E72.0");var subQ14=sQuery(id+"F12.wireOp",EDGE,"E72.1");var subQ16=sQuery(id+"F12.wireOp",EDGE,"E74.1");var subQ18=sQuery(id+"F12.wireOp",EDGE,"E74.8");Q0=qUnion([makeQuery(id+"F12.imprint","IMPRINT",FACE,{"disambiguationData":[TD([[makeQuery(id+"F12.imprint","IMPRINT",EDGE,{"derivedFrom":subQ7}),1.0]])]}),makeQuery(id+"F12.imprint","IMPRINT",FACE,{"disambiguationData":[TD([[makeQuery(id+"F12.imprint","IMPRINT",EDGE,{"derivedFrom":subQ14}),1.0]])]}),makeQuery(id+"F12.imprint","IMPRINT",FACE,{"disambiguationData":[TD([[makeQuery(id+"F12.imprint","IMPRINT",EDGE,{"derivedFrom":subQ16}),1.0]])]}),makeQuery(id+"F12.imprint","IMPRINT",FACE,{"disambiguationData":[TD([[makeQuery(id+"F12.imprint","IMPRINT",EDGE,{"derivedFrom":subQ18}),-1.0]])]})]);}
            var Q1;
            Q1=makeQuery(id+"F5.boolean.opBoolean","SPLIT",FACE,{"disambiguationData":[TD([makeQuery(id+"F5.opExtrude","SWEPT_FACE",FACE,{"disambiguationData":[OSD([sQuery(id+"F4.wireOp",EDGE,"E41")])]})])],"derivedFrom":makeQuery(id+"F3.boolean.opBoolean","COPY",FACE,{"derivedFrom":makeQuery(id+"F3.opExtrude","CAP_FACE",FACE,{"disambiguationData":[OSD([sQuery(id+"F0.wireOp",EDGE,"E25.0"),sQuery(id+"F0.wireOp",EDGE,"E25.1"),sQuery(id+"F0.wireOp",EDGE,"E25.2"),sQuery(id+"F0.wireOp",EDGE,"E25.3"),sQuery(id+"F0.wireOp",EDGE,"E25.4"),sQuery(id+"F0.wireOp",EDGE,"E25.5"),sQuery(id+"F0.wireOp",EDGE,"E25.6"),sQuery(id+"F0.wireOp",EDGE,"E25.7")])],"isStart":false})})});
            extrude(context, id + "F13", {"entities" : qUnion([Q0]), "operationType" : NewBodyOperationType.REMOVE, "endBound" : BoundingType.UP_TO_SURFACE, "endBoundEntityFace" : qUnion([Q1]), "depth" : 25 * mm});
        }
        {
            var Q0;
            Q0=makeQuery(id+"F3.boolean.opBoolean","COPY",EDGE,{"derivedFrom":makeQuery(id+"F3.opExtrude","CAP_EDGE",EDGE,{"disambiguationData":[OSD([sQuery(id+"F0.wireOp",EDGE,"E25.6")])],"isStart":false})});
            var Q1;
            Q1=makeQuery(id+"F8.boolean.opBoolean","INTERSECT",EDGE,{"derivedFrom":[makeQuery(id+"F5.opExtrude","SWEPT_FACE",FACE,{"disambiguationData":[OSD([sQuery(id+"F4.wireOp",EDGE,"E30")])]}),makeQuery(id+"F8.opExtrude","CAP_FACE",FACE,{"disambiguationData":[OSD([sQuery(id+"F7.wireOp",EDGE,"E67")])],"isStart":false})]});
            var Q2;
            Q2=makeQuery(id+"F8.boolean.opBoolean","INTERSECT",EDGE,{"disambiguationData":[OD(1.0)],"derivedFrom":[makeQuery(id+"F5.opExtrude","SWEPT_FACE",FACE,{"disambiguationData":[OSD([sQuery(id+"F4.wireOp",EDGE,"E30")])]}),makeQuery(id+"F8.opExtrude","SWEPT_FACE",FACE,{"disambiguationData":[OSD([sQuery(id+"F7.wireOp",EDGE,"E67")])]})]});
            var Q3;
            {var subQ0=sQuery(id+"F4.wireOp",EDGE,"E30");Q3=makeQuery(id+"F8.boolean.opBoolean","SPLIT",EDGE,{"disambiguationData":[TD([makeQuery(id+"F5.opExtrude","SWEPT_FACE",FACE,{"disambiguationData":[OSD([sQuery(id+"F4.wireOp",EDGE,"E35.filletArc")])]})])],"derivedFrom":makeQuery(id+"F5.opExtrude","CAP_EDGE",EDGE,{"disambiguationData":[OSD([subQ0])],"isStart":false})});}
            var Q4;
            {var subQ0=sQuery(id+"F0.wireOp",EDGE,"E25.7");var subQ1=sQuery(id+"F0.wireOp",EDGE,"E25.1");var subQ2=sQuery(id+"F0.wireOp",EDGE,"E25.6");var subQ3=sQuery(id+"F0.wireOp",EDGE,"E25.5");var subQ4=sQuery(id+"F0.wireOp",EDGE,"E25.4");var subQ5=sQuery(id+"F0.wireOp",EDGE,"E25.0");var subQ6=sQuery(id+"F0.wireOp",EDGE,"E25.2");var subQ7=sQuery(id+"F0.wireOp",EDGE,"E25.3");Q4=makeQuery(id+"F8.boolean.opBoolean","INTERSECT",EDGE,{"derivedFrom":[makeQuery(id+"F5.boolean.opBoolean","SPLIT",FACE,{"disambiguationData":[TD([makeQuery(id+"F2.opExtrude","SWEPT_FACE",FACE,{"disambiguationData":[OSD([subQ5])]})])],"derivedFrom":makeQuery(id+"F3.boolean.opBoolean","COPY",FACE,{"derivedFrom":makeQuery(id+"F3.opExtrude","CAP_FACE",FACE,{"disambiguationData":[OSD([subQ5,subQ1,subQ6,subQ7,subQ4,subQ3,subQ2,subQ0])],"isStart":false})})}),makeQuery(id+"F8.opExtrude","SWEPT_FACE",FACE,{"disambiguationData":[OSD([sQuery(id+"F7.wireOp",EDGE,"E67")])]})]});}
            var Q5;
            Q5=makeQuery(id+"F8.boolean.opBoolean","INTERSECT",EDGE,{"disambiguationData":[OD(0.0)],"derivedFrom":[makeQuery(id+"F5.opExtrude","SWEPT_FACE",FACE,{"disambiguationData":[OSD([sQuery(id+"F4.wireOp",EDGE,"E30")])]}),makeQuery(id+"F8.opExtrude","SWEPT_FACE",FACE,{"disambiguationData":[OSD([sQuery(id+"F7.wireOp",EDGE,"E67")])]})]});
            fillet(context, id + "F14", {"entities" : qUnion([Q0, Q1, Q2, Q3, Q4, Q5]), "radius" : 3 * mm, "tangentPropagation" : true, "allowEdgeOverflow" : false});
        }
        {
            var Q0;
            Q0=makeQuery(id+"F1.opExtrude","CAP_EDGE",EDGE,{"disambiguationData":[OSD([sQuery(id+"F0.wireOp",EDGE,"E1.bottom")])],"isStart":false});
            fillet(context, id + "F15", {"entities" : qUnion([Q0]), "radius" : 2 * mm, "tangentPropagation" : true, "allowEdgeOverflow" : false});
        }
        {
            var Q0;
            {var subQ0=sQuery(id+"F0.wireOp",EDGE,"E22.filletArc");var subQ1=sQuery(id+"F0.wireOp",EDGE,"E7");var subQ2=sQuery(id+"F0.wireOp",EDGE,"E6");var subQ3=sQuery(id+"F0.wireOp",EDGE,"E5");var subQ4=sQuery(id+"F0.wireOp",EDGE,"E4");var subQ5=sQuery(id+"F0.wireOp",EDGE,"E1.bottom");var subQ6=sQuery(id+"F0.wireOp",EDGE,"E21.filletArc");var subQ7=sQuery(id+"F0.wireOp",EDGE,"E1.top");var subQ8=sQuery(id+"F0.wireOp",EDGE,"E1.left");var subQ9=sQuery(id+"F0.wireOp",EDGE,"E1.right");var subQ10=sQuery(id+"F0.wireOp",EDGE,"E23.filletArc");var subQ11=sQuery(id+"F0.wireOp",EDGE,"E24.filletArc");Q0=makeQuery(id+"F2.boolean.opBoolean","SPLIT",FACE,{"disambiguationData":[TD([makeQuery(id+"F1.opExtrude","SWEPT_FACE",FACE,{"disambiguationData":[OSD([subQ5])]})])],"derivedFrom":makeQuery(id+"F1.opExtrude","CAP_FACE",FACE,{"disambiguationData":[OSD([subQ5,subQ7,subQ8,subQ9,subQ4,subQ3,subQ2,subQ1,subQ6,subQ0,subQ10,subQ11])],"isStart":true})});}
            var sketch = newSketch(context, id + "F16", { "sketchPlane" : qUnion([Q0])});
            skLineSegment(sketch, "E79", {"start": v(-33, 74.25) * mm, "end": v(-15, 92.25) * mm});
            skLineSegment(sketch, "E80", {"start": v(-15, 92.25) * mm, "end": v(-15, 104.25) * mm});
            skArc(sketch, "E81", {"start": v(15, 104.25) * mm, "mid": v(0, 119.25) * mm, "end": v(-15, 104.25) * mm});
            skLineSegment(sketch, "E82", {"start": v(15, 104.25) * mm, "end": v(15, 92.25) * mm});
            skLineSegment(sketch, "E83", {"start": v(15, 92.25) * mm, "end": v(33, 74.25) * mm});
            skCircle(sketch, "E84", {"center": v(0, 104.25) * mm, "radius": 6 * mm});
            skLineSegment(sketch, "E85", {"start": v(0, 104.25) * mm, "end": v(0, 74.25) * mm, "construction": true});
            skLineSegment(sketch, "E86", {"start": v(-64.25, 74.25) * mm, "end": v(64.25, 74.25) * mm});
            skLineSegment(sketch, "E87", {"start": v(74.25, 64.25) * mm, "end": v(74.25, -64.25) * mm});
            skLineSegment(sketch, "E88", {"start": v(64.25, -74.25) * mm, "end": v(-64.25, -74.25) * mm});
            skLineSegment(sketch, "E89", {"start": v(-74.25, -64.25) * mm, "end": v(-74.25, 64.25) * mm});
            skArc(sketch, "E90", {"start": v(-64.25, 74.25) * mm, "mid": v(-71.32, 71.32) * mm, "end": v(-74.25, 64.25) * mm});
            skArc(sketch, "E91", {"start": v(74.25, 64.25) * mm, "mid": v(71.32, 71.32) * mm, "end": v(64.25, 74.25) * mm});
            skArc(sketch, "E92", {"start": v(64.25, -74.25) * mm, "mid": v(71.32, -71.32) * mm, "end": v(74.25, -64.25) * mm});
            skArc(sketch, "E93", {"start": v(-74.25, -64.25) * mm, "mid": v(-71.32, -71.32) * mm, "end": v(-64.25, -74.25) * mm});
            skArc(sketch, "E94.MirrorCS", {"start": v(15, -104.25) * mm, "mid": v(0, -119.25) * mm, "end": v(-15, -104.25) * mm});
            skLineSegment(sketch, "E95.MirrorCS", {"start": v(-15, -92.25) * mm, "end": v(-15, -104.25) * mm});
            skLineSegment(sketch, "E96.MirrorCS", {"start": v(-33, -74.25) * mm, "end": v(-15, -92.25) * mm});
            skLineSegment(sketch, "E97.MirrorCS", {"start": v(0, -104.25) * mm, "end": v(0, -74.25) * mm, "construction": true});
            skCircle(sketch, "E98.MirrorC", {"center": v(0, -104.25) * mm, "radius": 6 * mm});
            skLineSegment(sketch, "E99.MirrorCS", {"start": v(15, -92.25) * mm, "end": v(33, -74.25) * mm});
            skLineSegment(sketch, "E100.MirrorCS", {"start": v(15, -104.25) * mm, "end": v(15, -92.25) * mm});
            skLineSegment(sketch, "E101", {"start": v(-74.25, 0) * mm, "end": v(74.25, 0) * mm, "construction": true});
            skLineSegment(sketch, "E102", {"start": v(-60, 38.83) * mm, "end": v(-60, -38.83) * mm});
            skLineSegment(sketch, "E103", {"start": v(60, 38.83) * mm, "end": v(60, -38.83) * mm});
            skArc(sketch, "E104", {"start": v(-54.26, 47.88) * mm, "mid": v(-58.44, 44.2) * mm, "end": v(-60, 38.83) * mm});
            skArc(sketch, "E105", {"start": v(60, 38.83) * mm, "mid": v(58.44, 44.2) * mm, "end": v(54.26, 47.88) * mm});
            skArc(sketch, "E106", {"start": v(-60, -38.83) * mm, "mid": v(-58.44, -44.2) * mm, "end": v(-54.26, -47.88) * mm});
            skArc(sketch, "E107", {"start": v(54.26, -47.88) * mm, "mid": v(58.44, -44.2) * mm, "end": v(60, -38.83) * mm});
            skArc(sketch, "E108", {"start": v(-54.26, -47.88) * mm, "mid": v(0, -59.89) * mm, "end": v(54.26, -47.88) * mm});
            skArc(sketch, "E109.MirrorCS", {"start": v(-54.26, 47.88) * mm, "mid": v(0, 59.89) * mm, "end": v(54.26, 47.88) * mm});
            skCircle(sketch, "E110", {"center": v(-60, 60) * mm, "radius": 3.99 * mm});
            skCircle(sketch, "E111", {"center": v(60, 60) * mm, "radius": 3.96 * mm});
            skCircle(sketch, "E112", {"center": v(60, -60) * mm, "radius": 3.89 * mm});
            skCircle(sketch, "E113", {"center": v(-60, -60) * mm, "radius": 3.84 * mm});
            skSolve(sketch);
        }
        {
            var Q0;
            Q0 = qSketchRegion(id + "F16", true);
            var Q1;
            Q1=makeQuery(id+"F2.opExtrude","CAP_FACE",FACE,{"disambiguationData":[OSD([sQuery(id+"F0.wireOp",EDGE,"E12"),sQuery(id+"F0.wireOp",EDGE,"E13"),sQuery(id+"F0.wireOp",EDGE,"E14"),sQuery(id+"F0.wireOp",EDGE,"E15"),sQuery(id+"F0.wireOp",EDGE,"E17.filletArc"),sQuery(id+"F0.wireOp",EDGE,"E18.filletArc"),sQuery(id+"F0.wireOp",EDGE,"E19.filletArc"),sQuery(id+"F0.wireOp",EDGE,"E20.filletArc"),sQuery(id+"F0.wireOp",EDGE,"E25.0"),sQuery(id+"F0.wireOp",EDGE,"E25.1"),sQuery(id+"F0.wireOp",EDGE,"E25.2"),sQuery(id+"F0.wireOp",EDGE,"E25.3"),sQuery(id+"F0.wireOp",EDGE,"E25.4"),sQuery(id+"F0.wireOp",EDGE,"E25.5"),sQuery(id+"F0.wireOp",EDGE,"E25.6"),sQuery(id+"F0.wireOp",EDGE,"E25.7")])],"isStart":false});
            extrude(context, id + "F17", {"entities" : qUnion([Q0]), "endBound" : BoundingType.UP_TO_SURFACE, "endBoundEntityFace" : qUnion([Q1]), "depth" : 25 * mm});
        }
    });
